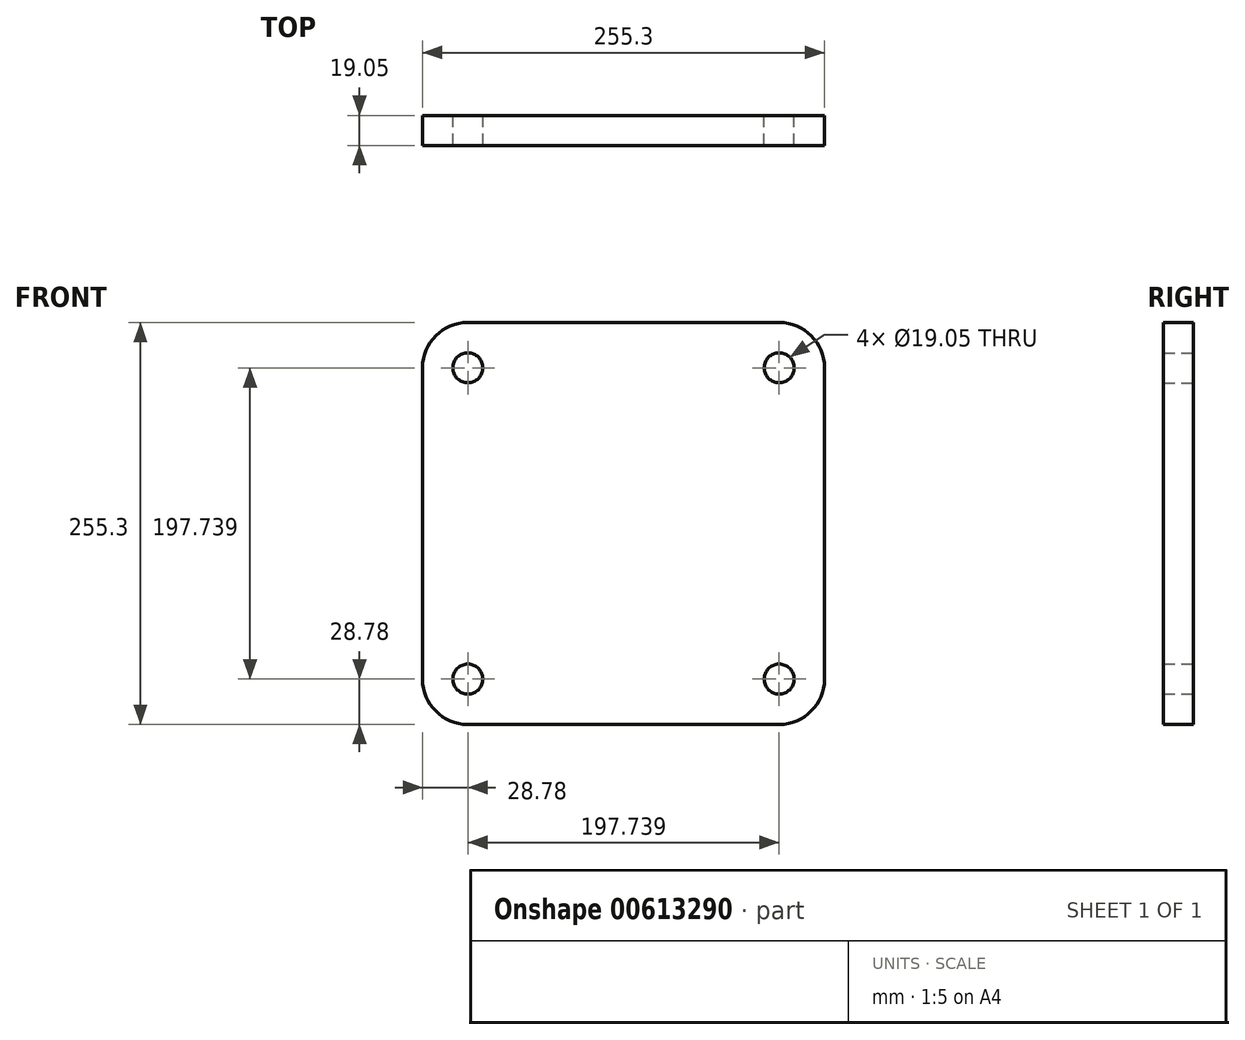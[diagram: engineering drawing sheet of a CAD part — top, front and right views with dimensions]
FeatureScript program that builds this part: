
annotation { "Feature Type Name" : "Feature", "Feature Type Description" : "" }
export const myFeature = defineFeature(function(context is Context, id is Id, definition is map)
    precondition{}
    {
        {
            var Q0;
            Q0=qCreatedBy(makeId("Front.planeOp"),FACE);
            var sketch = newSketch(context, id + "F0", { "sketchPlane" : qUnion([Q0])});
            skLineSegment(sketch, "E0.bottom", {"start": v(28.78, 0) * mm, "end": v(226.52, 0) * mm});
            skLineSegment(sketch, "E0.top", {"start": v(28.78, 255.3) * mm, "end": v(226.52, 255.3) * mm});
            skLineSegment(sketch, "E0.left", {"start": v(0, 28.78) * mm, "end": v(0, 226.52) * mm});
            skLineSegment(sketch, "E0.right", {"start": v(255.3, 28.78) * mm, "end": v(255.3, 226.52) * mm});
            skCircle(sketch, "E1", {"center": v(28.78, 28.78) * mm, "radius": 9.53 * mm});
            skCircle(sketch, "E2.0.1.0", {"center": v(28.78, 226.52) * mm, "radius": 9.53 * mm});
            skCircle(sketch, "E2.1.0.0", {"center": v(226.52, 28.78) * mm, "radius": 9.53 * mm});
            skCircle(sketch, "E2.1.1.0", {"center": v(226.52, 226.52) * mm, "radius": 9.53 * mm});
            skLineSegment(sketch, "E2.direction1", {"start": v(28.78, 28.78) * mm, "end": v(226.52, 28.78) * mm, "construction": true});
            skLineSegment(sketch, "E2.direction2", {"start": v(28.78, 28.78) * mm, "end": v(28.78, 226.52) * mm, "construction": true});
            skPoint(sketch, "E3.visualSharp", {"position": v(0, 255.3) * mm});
            skArc(sketch, "E3.filletArc", {"start": v(28.78, 255.3) * mm, "mid": v(8.43, 246.87) * mm, "end": v(0, 226.52) * mm});
            skPoint(sketch, "E4.visualSharp", {"position": v(255.3, 255.3) * mm});
            skArc(sketch, "E4.filletArc", {"start": v(255.3, 226.52) * mm, "mid": v(246.87, 246.87) * mm, "end": v(226.52, 255.3) * mm});
            skPoint(sketch, "E5.visualSharp", {"position": v(255.3, 0) * mm});
            skArc(sketch, "E5.filletArc", {"start": v(226.52, 0) * mm, "mid": v(246.87, 8.43) * mm, "end": v(255.3, 28.78) * mm});
            skPoint(sketch, "E6.visualSharp", {"position": v(0, 0) * mm});
            skArc(sketch, "E6.filletArc", {"start": v(0, 28.78) * mm, "mid": v(8.43, 8.43) * mm, "end": v(28.78, 0) * mm});
            skSolve(sketch);
        }
        {
            var Q0;
            Q0=makeQuery(id+"F0.imprint","IMPRINT",FACE,{"disambiguationData":[TD([[makeQuery(id+"F0.imprint","IMPRINT",EDGE,{"derivedFrom":sQuery(id+"F0.wireOp",EDGE,"1qnOmSaI-Xxrh-0afN-UeiG-LIwPmX5NAdLk.bottom")}),1.0]])]});
            var Q1;
            Q1=makeQuery(id+"F0.imprint","IMPRINT",FACE,{"disambiguationData":[TD([[makeQuery(id+"F0.imprint","IMPRINT",EDGE,{"derivedFrom":sQuery(id+"F0.wireOp",EDGE,"E0.bottom")}),1.0]])]});
            extrude(context, id + "F1", {"entities" : qUnion([Q0, Q1]), "depth" : 19.05 * mm, "offsetDistance" : 25.4 * mm});
        }
    });
